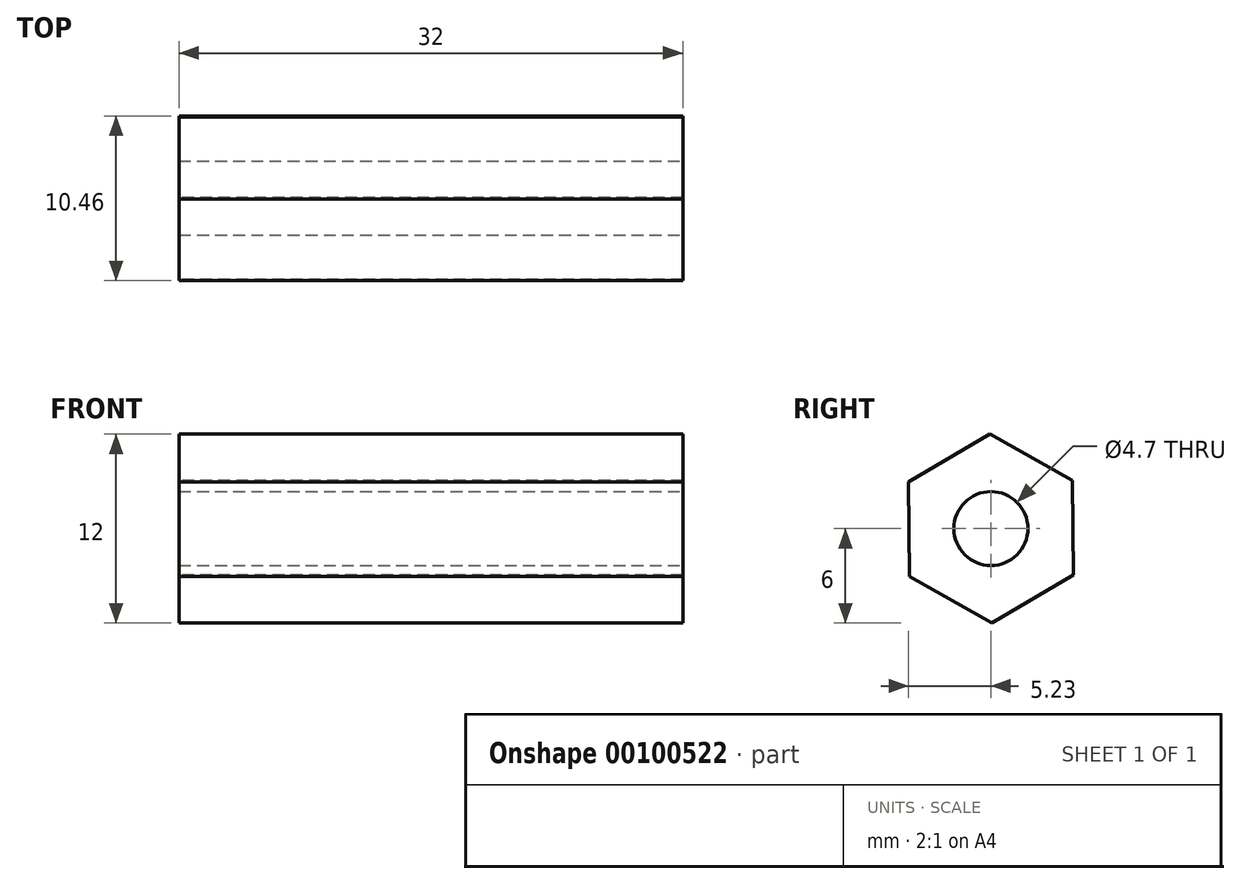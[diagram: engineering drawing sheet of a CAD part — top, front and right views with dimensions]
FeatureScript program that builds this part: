
annotation { "Feature Type Name" : "Feature", "Feature Type Description" : "" }
export const myFeature = defineFeature(function(context is Context, id is Id, definition is map)
    precondition{}
    {
        {
            var Q0;
            Q0=qCreatedBy(makeId("Right.planeOp"),FACE);
            var sketch = newSketch(context, id + "F0", { "sketchPlane" : qUnion([Q0])});
            skCircle(sketch, "E0.cCircle", {"center": v(0, 0) * mm, "radius": 5.2 * mm, "construction": true});
            skLineSegment(sketch, "E0.0", {"start": v(5.23, -2.95) * mm, "end": v(0.06, -6) * mm});
            skLineSegment(sketch, "E0.1", {"start": v(0.06, -6) * mm, "end": v(-5.17, -3.05) * mm});
            skLineSegment(sketch, "E0.2", {"start": v(-5.17, -3.05) * mm, "end": v(-5.23, 2.95) * mm});
            skLineSegment(sketch, "E0.3", {"start": v(-5.23, 2.95) * mm, "end": v(-0.06, 6) * mm});
            skLineSegment(sketch, "E0.4", {"start": v(-0.06, 6) * mm, "end": v(5.17, 3.05) * mm});
            skLineSegment(sketch, "E0.5", {"start": v(5.17, 3.05) * mm, "end": v(5.23, -2.95) * mm});
            skPoint(sketch, "E0.0.midPoint", {"position": v(2.64, -4.47) * mm});
            skSolve(sketch);
        }
        {
            var Q0;
            Q0=makeQuery(id+"F0.imprint","IMPRINT",FACE,{"disambiguationData":[TD([[makeQuery(id+"F0.imprint","IMPRINT",EDGE,{"derivedFrom":sQuery(id+"F0.wireOp",EDGE,"E0.0")}),-1.0]])]});
            extrude(context, id + "F1", {"entities" : qUnion([Q0]), "depth" : 32 * mm});
        }
        {
            var Q0;
            Q0=makeQuery(id+"F1.opExtrude","CAP_FACE",FACE,{"disambiguationData":[OSD([sQuery(id+"F0.wireOp",EDGE,"E0.0"),sQuery(id+"F0.wireOp",EDGE,"E0.1"),sQuery(id+"F0.wireOp",EDGE,"E0.2"),sQuery(id+"F0.wireOp",EDGE,"E0.3"),sQuery(id+"F0.wireOp",EDGE,"E0.4"),sQuery(id+"F0.wireOp",EDGE,"E0.5")])],"isStart":false});
            var sketch = newSketch(context, id + "F2", { "sketchPlane" : qUnion([Q0])});
            skCircle(sketch, "E1", {"center": v(0, 0) * mm, "radius": 3.5 * mm});
            skSolve(sketch);
        }
        {
            var Q0;
            Q0=sQuery(id+"F2.wireOp",VERTEX,"E1.center");
            var Q1;
            Q1=makeQuery(id+"F1.opExtrude","SWEPT_BODY",BODY,{"disambiguationData":[OSD([sQuery(id+"F0.wireOp",EDGE,"E0.0"),sQuery(id+"F0.wireOp",EDGE,"E0.1"),sQuery(id+"F0.wireOp",EDGE,"E0.2"),sQuery(id+"F0.wireOp",EDGE,"E0.3"),sQuery(id+"F0.wireOp",EDGE,"E0.4"),sQuery(id+"F0.wireOp",EDGE,"E0.5")])]});
            hole(context, id + "F3", {"style" : HoleStyle.SIMPLE, "endStyle" : HoleEndStyle.THROUGH, "holeDiameter" : 4.7 * mm, "locations" : qUnion([Q0]), "scope" : qUnion([Q1]), "isTappedThrough" : true});
        }
    });
